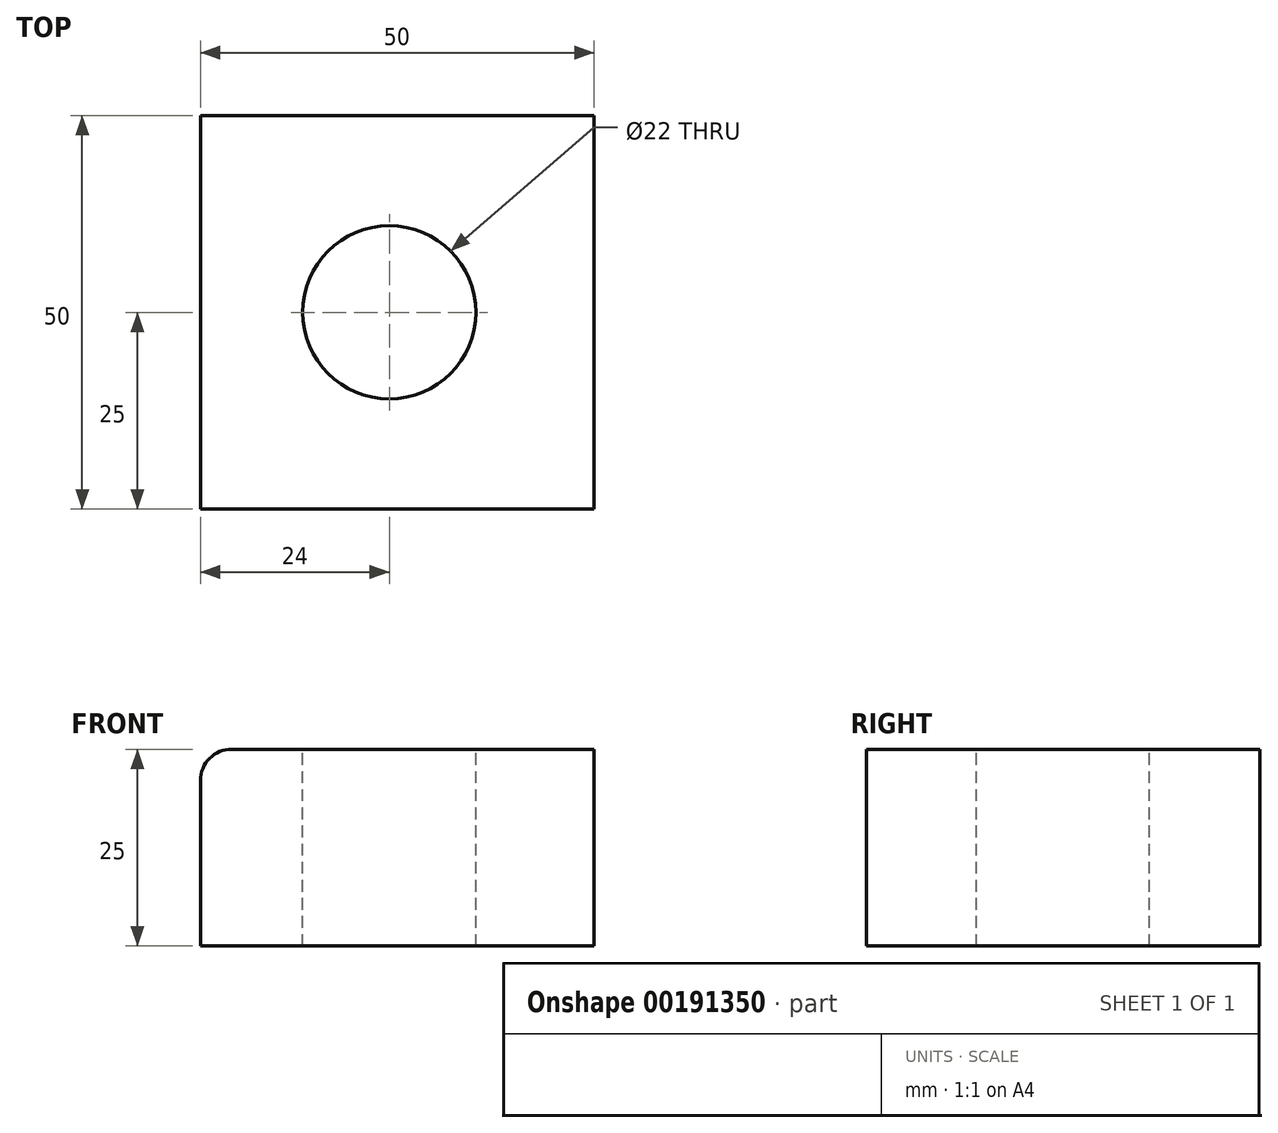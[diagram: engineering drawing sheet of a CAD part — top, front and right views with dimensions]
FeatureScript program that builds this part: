
annotation { "Feature Type Name" : "Feature", "Feature Type Description" : "" }
export const myFeature = defineFeature(function(context is Context, id is Id, definition is map)
    precondition{}
    {
        {
            var Q0;
            Q0=qCreatedBy(makeId("Front.planeOp"),FACE);
            var sketch = newSketch(context, id + "F0", { "sketchPlane" : qUnion([Q0])});
            skLineSegment(sketch, "E0", {"start": v(26, 0) * mm, "end": v(-24, 0) * mm});
            skLineSegment(sketch, "E1", {"start": v(-24, 0) * mm, "end": v(-24, -25) * mm});
            skLineSegment(sketch, "E2", {"start": v(-24, -25) * mm, "end": v(26, -25) * mm});
            skLineSegment(sketch, "E3", {"start": v(26, -25) * mm, "end": v(26, 0) * mm});
            skSolve(sketch);
        }
        {
            var Q0;
            Q0 = qSketchRegion(id + "F0", true);
            extrude(context, id + "F1", {"entities" : qUnion([Q0]), "endBound" : BoundingType.SYMMETRIC, "depth" : 50 * mm});
        }
        {
            var Q0;
            Q0=makeQuery(id+"F1.opExtrude","SWEPT_EDGE",EDGE,{"disambiguationData":[OSD([sQuery(id+"F0.wireOp",EDGE,"E0"),sQuery(id+"F0.wireOp",EDGE,"E1")])]});
            fillet(context, id + "F2", {"entities" : qUnion([Q0]), "radius" : 4 * mm, "tangentPropagation" : true, "allowEdgeOverflow" : false});
        }
        {
            var Q0;
            Q0=makeQuery(id+"F1.opExtrude","SWEPT_FACE",FACE,{"disambiguationData":[OSD([sQuery(id+"F0.wireOp",EDGE,"E0")])]});
            var sketch = newSketch(context, id + "F3", { "sketchPlane" : qUnion([Q0])});
            skCircle(sketch, "E4", {"center": v(0, 0) * mm, "radius": 11 * mm});
            skSolve(sketch);
        }
        {
            var Q0;
            Q0 = qSketchRegion(id + "F3", true);
            extrude(context, id + "F4", {"entities" : qUnion([Q0]), "operationType" : NewBodyOperationType.REMOVE, "endBound" : BoundingType.THROUGH_ALL, "oppositeDirection" : true, "depth" : 25 * mm});
        }
    });
